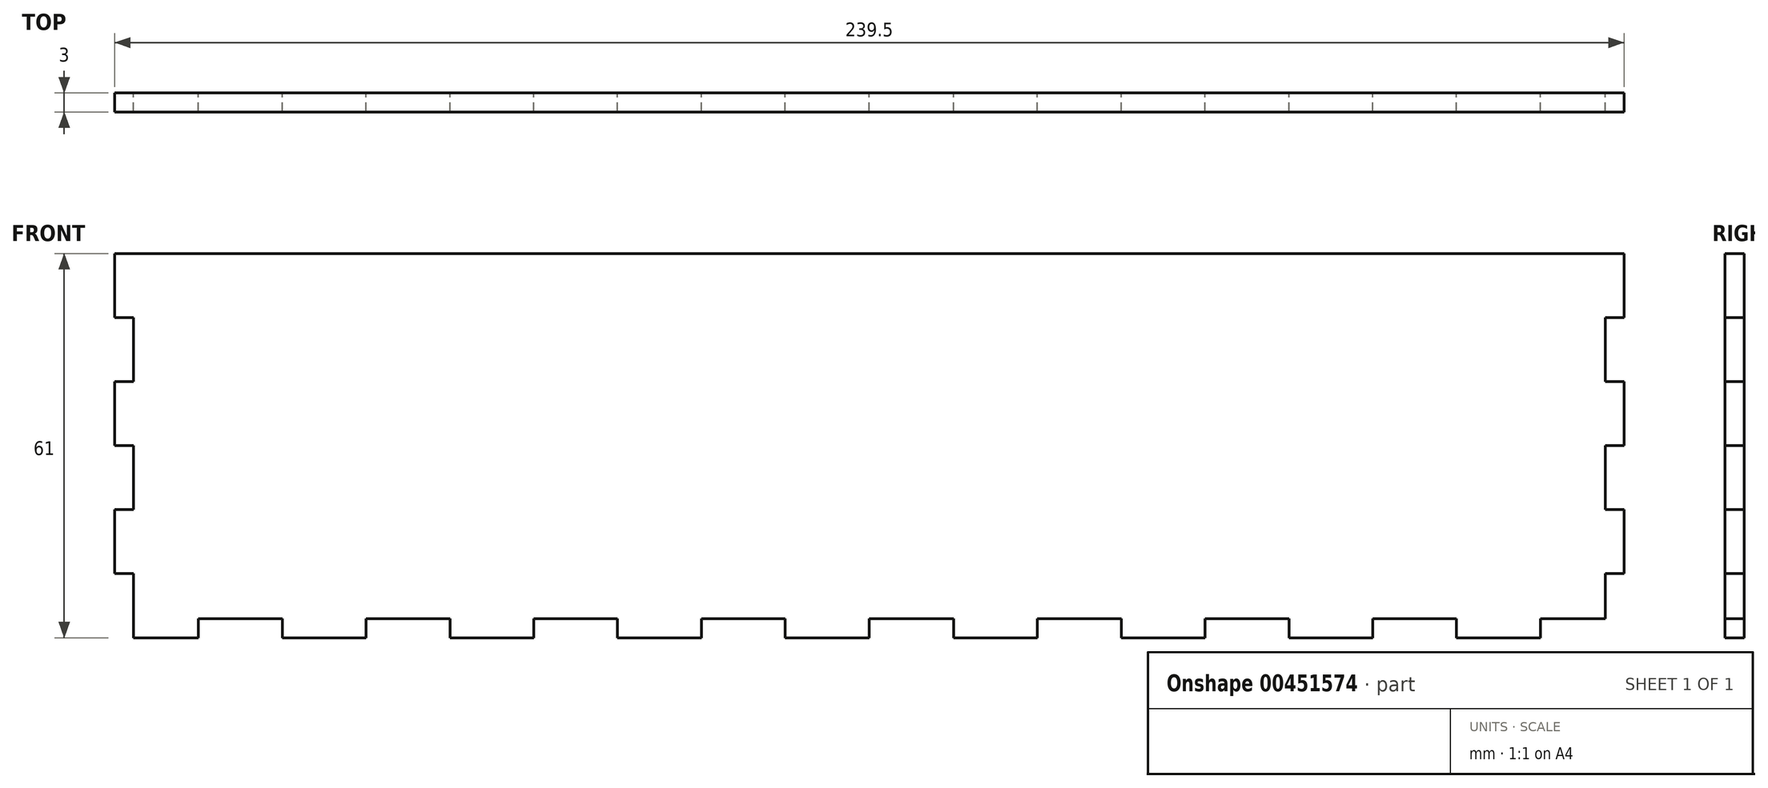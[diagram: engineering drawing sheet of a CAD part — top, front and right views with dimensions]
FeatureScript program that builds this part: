
annotation { "Feature Type Name" : "Feature", "Feature Type Description" : "" }
export const myFeature = defineFeature(function(context is Context, id is Id, definition is map)
    precondition{}
    {
        {
            var Q0;
            Q0=qCreatedBy(makeId("Front.planeOp"),FACE);
            var sketch = newSketch(context, id + "F0", { "sketchPlane" : qUnion([Q0])});
            skLineSegment(sketch, "E0.bottom", {"start": v(106.45, -30.5) * mm, "end": v(93.15, -30.5) * mm});
            skLineSegment(sketch, "E0.top", {"start": v(119.75, 30.5) * mm, "end": v(-119.75, 30.5) * mm});
            skLineSegment(sketch, "E0.right", {"start": v(-119.75, -20.33) * mm, "end": v(-119.75, -10.16) * mm});
            skPoint(sketch, "E0.middle", {"position": v(0, 0) * mm});
            skLineSegment(sketch, "E1.MirrorCS", {"start": v(-0.05, -30.5) * mm, "end": v(-0.05, -27.5) * mm});
            skLineSegment(sketch, "E2.MirrorCS", {"start": v(0.05, -30.5) * mm, "end": v(0.05, -27.5) * mm});
            skLineSegment(sketch, "E3.MirrorCS", {"start": v(-66.55, -30.5) * mm, "end": v(-66.55, -27.5) * mm});
            skLineSegment(sketch, "E4.MirrorCS", {"start": v(-79.85, -30.5) * mm, "end": v(-79.85, -27.5) * mm});
            skLineSegment(sketch, "E5.MirrorCS", {"start": v(-93.15, -30.5) * mm, "end": v(-93.15, -27.5) * mm});
            skLineSegment(sketch, "E6.MirrorCS", {"start": v(-106.45, -30.5) * mm, "end": v(-106.45, -27.5) * mm});
            skLineSegment(sketch, "E7.MirrorCS", {"start": v(-39.95, -30.5) * mm, "end": v(-39.95, -27.5) * mm});
            skLineSegment(sketch, "E8.MirrorCS", {"start": v(-26.65, -30.5) * mm, "end": v(-26.65, -27.5) * mm});
            skLineSegment(sketch, "E9.MirrorCS", {"start": v(-13.35, -30.5) * mm, "end": v(-13.35, -27.5) * mm});
            skLineSegment(sketch, "E10.MirrorCS", {"start": v(53.25, -30.5) * mm, "end": v(53.25, -27.5) * mm});
            skLineSegment(sketch, "E11.MirrorCS", {"start": v(93.15, -30.5) * mm, "end": v(93.15, -27.5) * mm});
            skLineSegment(sketch, "E12.MirrorCS", {"start": v(106.45, -30.5) * mm, "end": v(106.45, -27.5) * mm});
            skLineSegment(sketch, "E13.MirrorCS", {"start": v(39.95, -30.5) * mm, "end": v(39.95, -27.5) * mm});
            skLineSegment(sketch, "E14.MirrorCS", {"start": v(79.85, -30.5) * mm, "end": v(79.85, -27.5) * mm});
            skLineSegment(sketch, "E15.MirrorCS", {"start": v(26.65, -30.5) * mm, "end": v(26.65, -27.5) * mm});
            skLineSegment(sketch, "E16.MirrorCS", {"start": v(66.55, -30.5) * mm, "end": v(66.55, -27.5) * mm});
            skLineSegment(sketch, "E17.MirrorCS", {"start": v(13.35, -30.5) * mm, "end": v(13.35, -27.5) * mm});
            skLineSegment(sketch, "E18.MirrorCS", {"start": v(-53.25, -30.5) * mm, "end": v(-53.25, -27.5) * mm});
            skLineSegment(sketch, "E19.MirrorCS", {"start": v(-106.45, -27.5) * mm, "end": v(-93.15, -27.5) * mm});
            skLineSegment(sketch, "E20.trimOffspring", {"start": v(-106.45, -30.5) * mm, "end": v(-116.75, -30.5) * mm});
            skLineSegment(sketch, "E21.trimOffspring", {"start": v(-79.85, -27.5) * mm, "end": v(-66.55, -27.5) * mm});
            skLineSegment(sketch, "E22.trimOffspring", {"start": v(-79.85, -30.5) * mm, "end": v(-93.15, -30.5) * mm});
            skLineSegment(sketch, "E23.trimOffspring", {"start": v(-53.25, -27.5) * mm, "end": v(-39.95, -27.5) * mm});
            skLineSegment(sketch, "E24.trimOffspring", {"start": v(-53.25, -30.5) * mm, "end": v(-66.55, -30.5) * mm});
            skLineSegment(sketch, "E25.trimOffspring", {"start": v(-26.65, -27.5) * mm, "end": v(-13.35, -27.5) * mm});
            skLineSegment(sketch, "E26.trimOffspring", {"start": v(-26.65, -30.5) * mm, "end": v(-39.95, -30.5) * mm});
            skLineSegment(sketch, "E27.trimOffspring", {"start": v(-0.05, -27.5) * mm, "end": v(13.35, -27.5) * mm});
            skLineSegment(sketch, "E28.trimOffspring", {"start": v(0.05, -30.5) * mm, "end": v(-0.05, -30.5) * mm});
            skLineSegment(sketch, "E29.trimOffspring", {"start": v(0.05, -30.5) * mm, "end": v(-13.35, -30.5) * mm});
            skLineSegment(sketch, "E30.trimOffspring", {"start": v(26.65, -27.5) * mm, "end": v(39.95, -27.5) * mm});
            skLineSegment(sketch, "E31.trimOffspring", {"start": v(26.65, -30.5) * mm, "end": v(13.35, -30.5) * mm});
            skLineSegment(sketch, "E32.trimOffspring", {"start": v(53.25, -27.5) * mm, "end": v(66.55, -27.5) * mm});
            skLineSegment(sketch, "E33.trimOffspring", {"start": v(53.25, -30.5) * mm, "end": v(39.95, -30.5) * mm});
            skLineSegment(sketch, "E34.trimOffspring", {"start": v(79.85, -27.5) * mm, "end": v(93.15, -27.5) * mm});
            skLineSegment(sketch, "E35.trimOffspring", {"start": v(79.85, -30.5) * mm, "end": v(66.55, -30.5) * mm});
            skLineSegment(sketch, "E36.trimOffspring", {"start": v(106.45, -27.5) * mm, "end": v(116.75, -27.5) * mm});
            skLineSegment(sketch, "E37", {"start": v(-116.75, -30.5) * mm, "end": v(-116.75, -20.33) * mm});
            skLineSegment(sketch, "E38", {"start": v(-119.75, 20.33) * mm, "end": v(-116.75, 20.33) * mm});
            skLineSegment(sketch, "E39", {"start": v(-116.75, 10.17) * mm, "end": v(-119.75, 10.17) * mm});
            skLineSegment(sketch, "E40", {"start": v(-119.75, 0) * mm, "end": v(-116.75, 0) * mm});
            skLineSegment(sketch, "E41", {"start": v(-116.75, 0) * mm, "end": v(-116.75, -10.16) * mm});
            skLineSegment(sketch, "E42", {"start": v(-116.75, -10.16) * mm, "end": v(-119.75, -10.16) * mm});
            skLineSegment(sketch, "E43", {"start": v(-119.75, -20.33) * mm, "end": v(-116.75, -20.33) * mm});
            skLineSegment(sketch, "E44.trimOffspring", {"start": v(-119.75, 20.33) * mm, "end": v(-119.75, 30.5) * mm});
            skLineSegment(sketch, "E45.trimOffspring", {"start": v(-116.75, 10.17) * mm, "end": v(-116.75, 20.33) * mm});
            skLineSegment(sketch, "E46.trimOffspring", {"start": v(-119.75, 0) * mm, "end": v(-119.75, 10.17) * mm});
            skLineSegment(sketch, "E47.trimOffspring", {"start": v(-116.75, -10.16) * mm, "end": v(-116.75, 0) * mm});
            skLineSegment(sketch, "E48.MirrorCS", {"start": v(116.75, 0) * mm, "end": v(116.75, -10.16) * mm});
            skLineSegment(sketch, "E49.MirrorCS", {"start": v(116.75, -10.16) * mm, "end": v(116.75, 0) * mm});
            skLineSegment(sketch, "E50.MirrorCS", {"start": v(119.75, 0) * mm, "end": v(119.75, 10.17) * mm});
            skLineSegment(sketch, "E51.MirrorCS", {"start": v(116.75, -10.16) * mm, "end": v(119.75, -10.16) * mm});
            skLineSegment(sketch, "E52.MirrorCS", {"start": v(116.75, 10.17) * mm, "end": v(119.75, 10.17) * mm});
            skLineSegment(sketch, "E53.MirrorCS", {"start": v(119.75, 20.33) * mm, "end": v(119.75, 30.5) * mm});
            skLineSegment(sketch, "E54.MirrorCS", {"start": v(119.75, 20.33) * mm, "end": v(116.75, 20.33) * mm});
            skLineSegment(sketch, "E55.MirrorCS", {"start": v(119.75, 0) * mm, "end": v(116.75, 0) * mm});
            skLineSegment(sketch, "E56.MirrorCS", {"start": v(116.75, 10.17) * mm, "end": v(116.75, 20.33) * mm});
            skLineSegment(sketch, "E57.MirrorCS", {"start": v(116.75, -27.5) * mm, "end": v(116.75, -20.33) * mm});
            skLineSegment(sketch, "E58.MirrorCS", {"start": v(119.75, -20.33) * mm, "end": v(119.75, -10.16) * mm});
            skLineSegment(sketch, "E59.MirrorCS", {"start": v(119.75, -20.33) * mm, "end": v(116.75, -20.33) * mm});
            skSolve(sketch);
        }
        {
            var Q0;
            Q0=makeQuery(id+"F0.imprint","IMPRINT",FACE,{"disambiguationData":[TD([[makeQuery(id+"F0.imprint","IMPRINT",EDGE,{"derivedFrom":sQuery(id+"F0.wireOp",EDGE,"E0.bottom")}),-1.0]])]});
            extrude(context, id + "F1", {"entities" : qUnion([Q0]), "depth" : 3 * mm, "offsetDistance" : 25 * mm});
        }
    });
